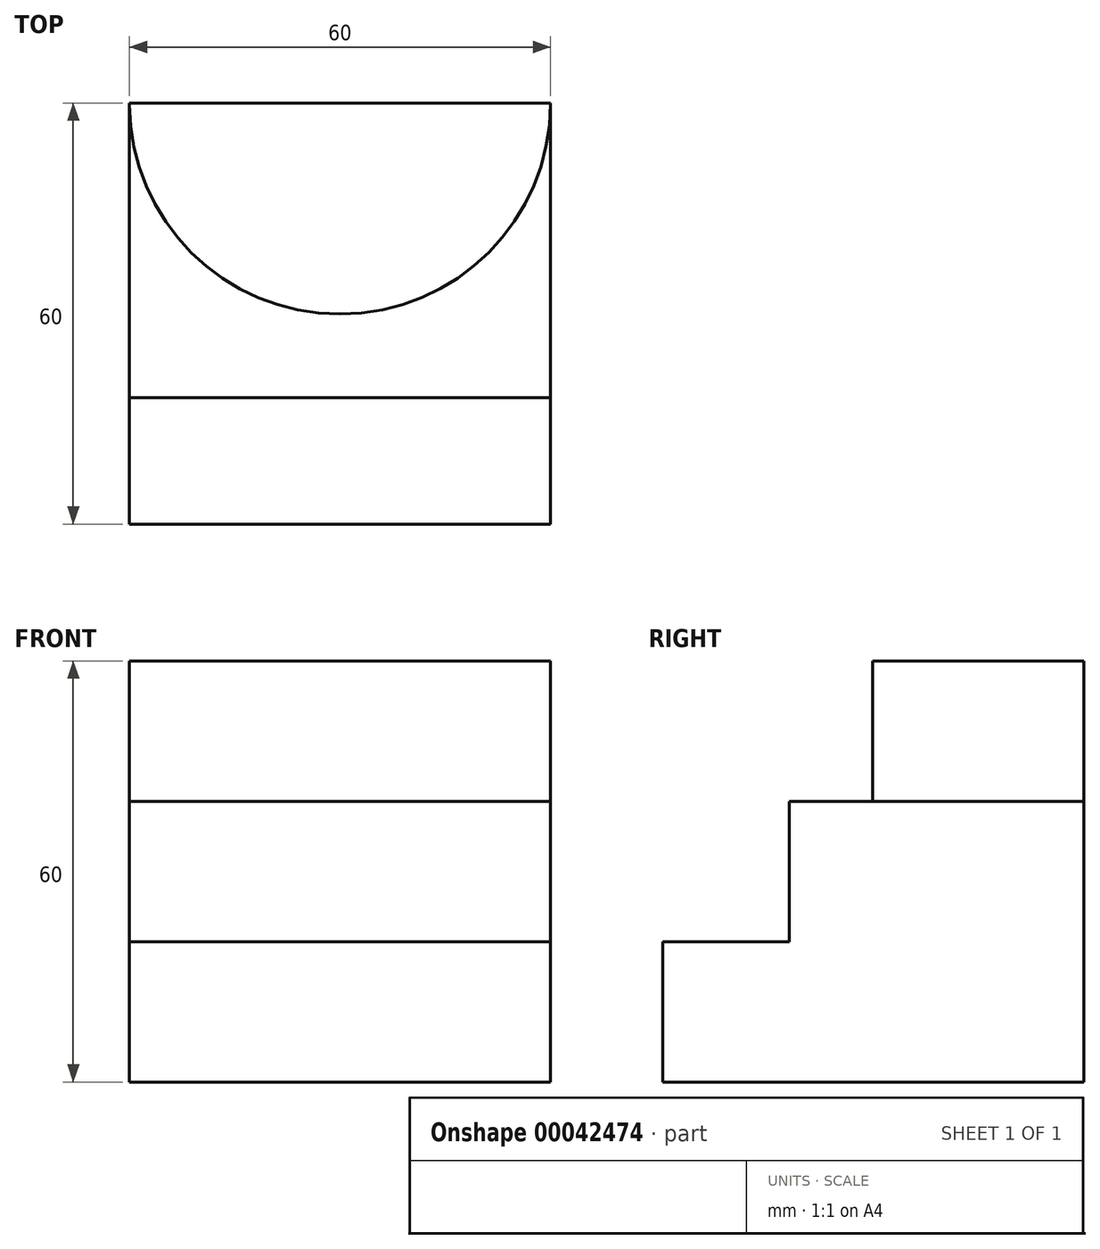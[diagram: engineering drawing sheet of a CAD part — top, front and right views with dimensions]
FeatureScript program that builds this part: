
annotation { "Feature Type Name" : "Feature", "Feature Type Description" : "" }
export const myFeature = defineFeature(function(context is Context, id is Id, definition is map)
    precondition{}
    {
        {
            var Q0;
            Q0=qCreatedBy(makeId("Top.planeOp"),FACE);
            var sketch = newSketch(context, id + "F0", { "sketchPlane" : qUnion([Q0])});
            skLineSegment(sketch, "E0.bottom", {"start": v(-30.92, 24.14) * mm, "end": v(29.08, 24.14) * mm});
            skLineSegment(sketch, "E0.top", {"start": v(-30.92, -35.86) * mm, "end": v(29.08, -35.86) * mm});
            skLineSegment(sketch, "E0.left", {"start": v(-30.92, 24.14) * mm, "end": v(-30.92, -35.86) * mm});
            skLineSegment(sketch, "E0.right", {"start": v(29.08, 24.14) * mm, "end": v(29.08, -35.86) * mm});
            skLineSegment(sketch, "E1", {"start": v(-30.92, -17.84) * mm, "end": v(29.08, -17.84) * mm});
            skSolve(sketch);
        }
        {
            var Q0;
            {var subQ2=sQuery(id+"F0.wireOp",EDGE,"E0.bottom");Q0=makeQuery(id+"F0.imprint","IMPRINT",FACE,{"disambiguationData":[TD([[makeQuery(id+"F0.imprint","IMPRINT",EDGE,{"derivedFrom":subQ2}),-1.0]])]});}
            var sketch = newSketch(context, id + "F1", { "sketchPlane" : qUnion([Q0])});
            skArc(sketch, "E2", {"start": v(-30.92, 24.14) * mm, "mid": v(-0.92, -5.94) * mm, "end": v(29.08, 24.14) * mm});
            skSolve(sketch);
        }
        {
            var Q0;
            {var subQ2=sQuery(id+"F0.wireOp",EDGE,"E0.bottom");var subQ10=makeQuery(id+"F0.imprint","IMPRINT",EDGE,{"derivedFrom":subQ2});Q0=makeQuery(id+"F1.imprint","IMPRINT",FACE,{"disambiguationData":[TD([[makeQuery(id+"F1.imprint","IMPRINT",EDGE,{"derivedFrom":subQ10}),-1.0]])]});}
            extrude(context, id + "F2", {"entities" : qUnion([Q0]), "depth" : 60 * mm});
        }
        {
            var Q0;
            {var subQ2=sQuery(id+"F0.wireOp",EDGE,"E0.bottom");Q0=makeQuery(id+"F0.imprint","IMPRINT",FACE,{"disambiguationData":[TD([[makeQuery(id+"F0.imprint","IMPRINT",EDGE,{"derivedFrom":subQ2}),-1.0]])]});}
            extrude(context, id + "F3", {"entities" : qUnion([Q0]), "operationType" : NewBodyOperationType.ADD, "depth" : 40 * mm});
        }
        {
            var Q0;
            {var subQ2=sQuery(id+"F0.wireOp",EDGE,"E0.top");Q0=makeQuery(id+"F0.imprint","IMPRINT",FACE,{"disambiguationData":[TD([[makeQuery(id+"F0.imprint","IMPRINT",EDGE,{"derivedFrom":subQ2}),1.0]])]});}
            extrude(context, id + "F4", {"entities" : qUnion([Q0]), "operationType" : NewBodyOperationType.ADD, "depth" : 20 * mm});
        }
    });
